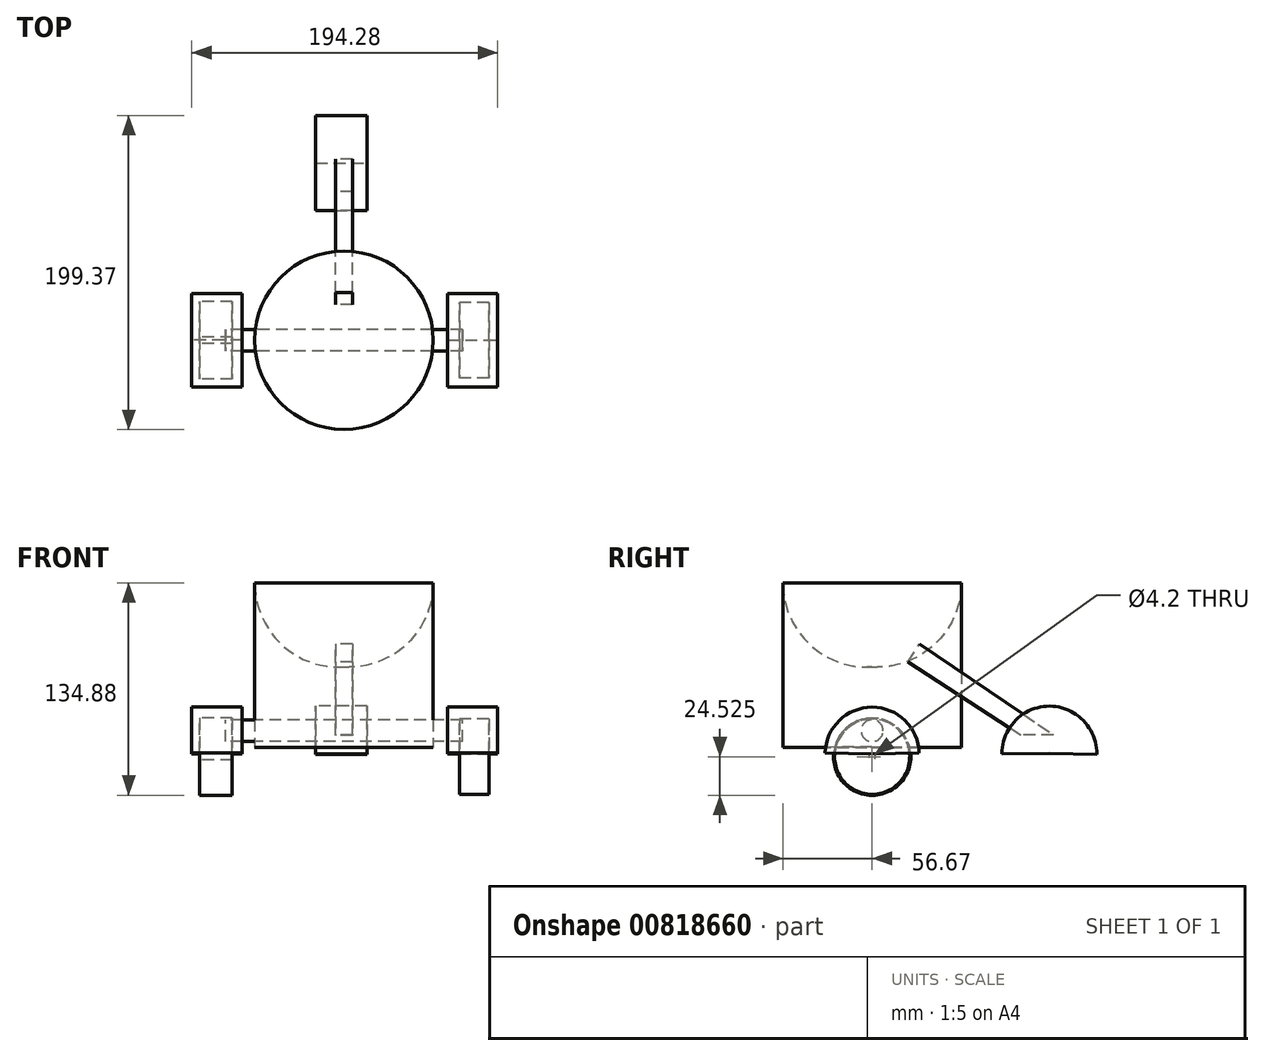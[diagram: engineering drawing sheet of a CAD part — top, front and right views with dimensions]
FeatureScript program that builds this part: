
annotation { "Feature Type Name" : "Feature", "Feature Type Description" : "" }
export const myFeature = defineFeature(function(context is Context, id is Id, definition is map)
    precondition{}
    {
        {
            var Q0;
            Q0=qCreatedBy(makeId("Front.planeOp"),FACE);
            var sketch = newSketch(context, id + "F0", { "sketchPlane" : qUnion([Q0])});
            skLineSegment(sketch, "E0", {"start": v(-56.67, 26.4) * mm, "end": v(-56.67, -78.17) * mm});
            skLineSegment(sketch, "E1", {"start": v(-56.67, -78.17) * mm, "end": v(0, -77.62) * mm});
            skLineSegment(sketch, "E2", {"start": v(0, -77.62) * mm, "end": v(0, 26.4) * mm});
            skPoint(sketch, "E3.orphan", {"position": v(0, 39.19) * mm});
            skArc(sketch, "E4", {"start": v(0, 79.74) * mm, "mid": v(-39.86, 65.31) * mm, "end": v(-56.67, 26.4) * mm});
            skLineSegment(sketch, "E5", {"start": v(0, 26.4) * mm, "end": v(0, 79.74) * mm});
            skSolve(sketch);
        }
        {
            var Q0;
            Q0 = qSketchRegion(id + "F0", true);
            var Q1;
            Q1=sQuery(id+"F0.wireOp",EDGE,"E2");
            revolve(context, id + "F1", {"surfaceOperationType" : NewSurfaceOperationType.NEW, "entities" : qUnion([Q0]), "axis" : qUnion([Q1]), "revolveType" : RevolveType.FULL});
        }
        {
            var Q0;
            Q0=qCreatedBy(makeId("Front.planeOp"),FACE);
            var sketch = newSketch(context, id + "F2", { "sketchPlane" : qUnion([Q0])});
            skLineSegment(sketch, "E6.bottom", {"start": v(-64.63, -52.48) * mm, "end": v(-96.67, -52.48) * mm});
            skLineSegment(sketch, "E6.top", {"start": v(-64.63, -82.3) * mm, "end": v(-96.67, -82.3) * mm});
            skLineSegment(sketch, "E6.left", {"start": v(-64.63, -52.48) * mm, "end": v(-64.63, -82.3) * mm});
            skLineSegment(sketch, "E6.right", {"start": v(-96.67, -52.48) * mm, "end": v(-96.67, -82.3) * mm});
            skLineSegment(sketch, "E7.bottom", {"start": v(65.7, -52.48) * mm, "end": v(97.6, -52.48) * mm});
            skLineSegment(sketch, "E7.top", {"start": v(65.7, -82.3) * mm, "end": v(97.6, -82.3) * mm});
            skLineSegment(sketch, "E7.left", {"start": v(65.7, -52.48) * mm, "end": v(65.7, -82.3) * mm});
            skLineSegment(sketch, "E7.right", {"start": v(97.6, -52.48) * mm, "end": v(97.6, -82.3) * mm});
            skSolve(sketch);
        }
        {
            var Q0;
            Q0 = qSketchRegion(id + "F2", true);
            var Q1;
            Q1=sQuery(id+"F2.wireOp",EDGE,"E6.top");
            revolve(context, id + "F3", {"surfaceOperationType" : NewSurfaceOperationType.NEW, "entities" : qUnion([Q0]), "axis" : qUnion([Q1]), "revolveType" : RevolveType.SYMMETRIC, "angle" : 177.53 * degree});
        }
        {
            var Q0;
            Q0=qCreatedBy(makeId("Right.planeOp"),FACE);
            var sketch = newSketch(context, id + "F4", { "sketchPlane" : qUnion([Q0])});
            skCircle(sketch, "E8", {"center": v(0, -67.44) * mm, "radius": 6.94 * mm});
            skSolve(sketch);
        }
        {
            var Q0;
            Q0 = qSketchRegion(id + "F4", true);
            extrude(context, id + "F5", {"entities" : qUnion([Q0]), "endBound" : BoundingType.SYMMETRIC, "depth" : 150.38 * mm, "offsetDistance" : 25.4 * mm});
        }
        {
            var Q0;
            Q0=qCreatedBy(makeId("Front.planeOp"),FACE);
            cPlane(context, id + "F6", {"entities" : qUnion([Q0]), "cplaneType" : CPlaneType.OFFSET, "offset" : 112.6 * mm, "oppositeDirection" : true, "width" : 152.4 * mm, "height" : 152.4 * mm});
        }
        {
            var Q0;
            Q0=qCreatedBy(id+"F6.planeOp",FACE);
            var sketch = newSketch(context, id + "F7", { "sketchPlane" : qUnion([Q0])});
            skLineSegment(sketch, "E9.bottom", {"start": v(-18.03, -51.85) * mm, "end": v(14.67, -51.85) * mm});
            skLineSegment(sketch, "E9.top", {"start": v(-18.03, -81.96) * mm, "end": v(14.67, -81.96) * mm});
            skLineSegment(sketch, "E9.left", {"start": v(-18.03, -51.85) * mm, "end": v(-18.03, -81.96) * mm});
            skLineSegment(sketch, "E9.right", {"start": v(14.67, -51.85) * mm, "end": v(14.67, -81.96) * mm});
            skSolve(sketch);
        }
        {
            var Q0;
            Q0 = qSketchRegion(id + "F7", true);
            var Q1;
            Q1=sQuery(id+"F7.wireOp",EDGE,"E9.top");
            revolve(context, id + "F8", {"surfaceOperationType" : NewSurfaceOperationType.NEW, "entities" : qUnion([Q0]), "axis" : qUnion([Q1]), "revolveType" : RevolveType.TWO_DIRECTIONS, "angle" : 90.18 * degree, "angleBack" : 269.14 * degree});
        }
        {
            var Q0;
            Q0=qCreatedBy(makeId("Right.planeOp"),FACE);
            var sketch = newSketch(context, id + "F9", { "sketchPlane" : qUnion([Q0])});
            skLineSegment(sketch, "E10", {"start": v(94.5, -70.27) * mm, "end": v(22.84, -23.64) * mm});
            skLineSegment(sketch, "E11", {"start": v(22.84, -23.64) * mm, "end": v(30.2, -12.32) * mm});
            skLineSegment(sketch, "E12", {"start": v(30.2, -12.32) * mm, "end": v(115.1, -69.97) * mm});
            skLineSegment(sketch, "E13", {"start": v(115.1, -69.97) * mm, "end": v(94.5, -70.27) * mm});
            skSolve(sketch);
        }
        {
            var Q0;
            Q0=makeQuery(id+"F9.imprint","IMPRINT",FACE,{"disambiguationData":[TD([[makeQuery(id+"F9.imprint","IMPRINT",EDGE,{"derivedFrom":sQuery(id+"F9.wireOp",EDGE,"E10")}),-1.0]])]});
            extrude(context, id + "F10", {"entities" : qUnion([Q0]), "endBound" : BoundingType.SYMMETRIC, "depth" : 10.78 * mm, "offsetDistance" : 25.4 * mm});
        }
        {
            var Q0;
            Q0=qCreatedBy(makeId("Front.planeOp"),FACE);
            var sketch = newSketch(context, id + "F11", { "sketchPlane" : qUnion([Q0])});
            skLineSegment(sketch, "E14.bottom", {"start": v(-91.54, -59.42) * mm, "end": v(-70.97, -59.42) * mm});
            skLineSegment(sketch, "E14.top", {"start": v(-91.54, -81.85) * mm, "end": v(-70.97, -81.85) * mm});
            skLineSegment(sketch, "E14.left", {"start": v(-91.54, -59.42) * mm, "end": v(-91.54, -81.85) * mm});
            skLineSegment(sketch, "E14.right", {"start": v(-70.97, -59.42) * mm, "end": v(-70.97, -81.85) * mm});
            skLineSegment(sketch, "E15.bottom", {"start": v(73.3, -60.07) * mm, "end": v(92.11, -60.07) * mm});
            skLineSegment(sketch, "E15.top", {"start": v(73.3, -83.95) * mm, "end": v(92.11, -83.95) * mm});
            skLineSegment(sketch, "E15.left", {"start": v(73.3, -60.07) * mm, "end": v(73.3, -83.95) * mm});
            skLineSegment(sketch, "E15.right", {"start": v(92.11, -60.07) * mm, "end": v(92.11, -83.95) * mm});
            skSolve(sketch);
        }
        {
            var Q0;
            Q0 = qSketchRegion(id + "F11", true);
            var Q1;
            Q1=sQuery(id+"F11.wireOp",EDGE,"E15.top");
            revolve(context, id + "F12", {"surfaceOperationType" : NewSurfaceOperationType.NEW, "entities" : qUnion([Q0]), "axis" : qUnion([Q1]), "revolveType" : RevolveType.FULL});
        }
    });
